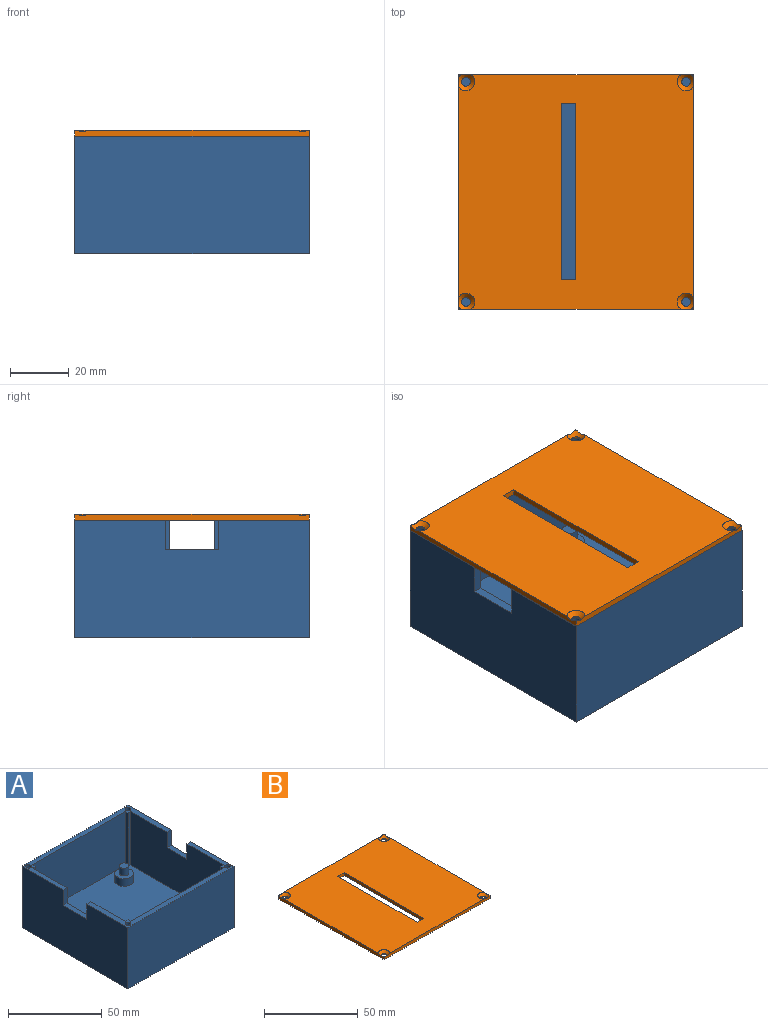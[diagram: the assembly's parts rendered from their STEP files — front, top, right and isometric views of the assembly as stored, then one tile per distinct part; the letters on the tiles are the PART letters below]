
ASSEMBLY  parts=2 mates=1
PART A: 50 faces, bbox 80x80x40 mm
  f0: plane 80x32.5mm, normal (0,0,1), area 406.4mm2, adj f1,f2,f4,f5,f6,f9,f10,f11
  f1: plane 80x40mm, normal (1,0,0), area 3050mm2, adj f0,f3,f5,f7,f8,f31,f32,f33
  f2: plane 70x35mm, normal (-1,0,0), area 2300mm2, adj f0,f3,f9,f18,f19,f31,f32,f33
  f3: plane 80x32.5mm, normal (0,0,1), area 406.4mm2, adj f1,f2,f4,f6,f7,f14,f15,f16
  f4: plane 70x35mm, normal (1,0,0), area 2270mm2, adj f0,f3,f13,f14,f19,f28,f29,f30
  f5: plane 80x40mm, normal (0,1,0), area 3200mm2, adj f0,f1,f6,f8
  f6: plane 80x40mm, normal (-1,0,0), area 3020mm2, adj f0,f3,f5,f7,f8,f28,f29,f30
  f7: plane 80x40mm, normal (0,-1,0), area 3200mm2, adj f1,f3,f6,f8
  f8: plane 80x80mm, normal (0,0,-1), area 6400mm2, adj f1,f5,f6,f7
  f9: plane 35x2mm, normal (0,-1,0), area 70mm2, adj f0,f2,f10,f19
  f10: plane 35x2mm, normal (-1,0,0), area 70mm2, adj f0,f9,f11,f19
  f11: plane 70x35mm, normal (0,-1,0), area 2450mm2, adj f0,f10,f12,f19
  f12: plane 35x2mm, normal (1,0,0), area 70mm2, adj f0,f11,f13,f19
  f13: plane 35x2mm, normal (0,-1,0), area 70mm2, adj f0,f4,f12,f19
  f14: plane 35x2mm, normal (0,1,0), area 70mm2, adj f3,f4,f15,f19
  f15: plane 35x2mm, normal (1,0,0), area 70mm2, adj f3,f14,f16,f19
  f16: plane 70x35mm, normal (0,1,0), area 2450mm2, adj f3,f15,f17,f19
  f17: plane 35x2mm, normal (-1,0,0), area 70mm2, adj f3,f16,f18,f19
  f18: plane 35x2mm, normal (0,1,0), area 70mm2, adj f2,f3,f17,f19
  f19: plane 74x74mm, normal (0,0,1), area 5145.8mm2, adj f2,f4,f9,f10,f11,f12,f13,f14
  f20: cylinder r=1.5mm len=9mm, axis (0,0,1), area 84.8mm2, adj f0,f21
  f21: plane 3x3mm, normal (0,0,1), area 7.1mm2, adj f20
  f22: cylinder r=1.5mm len=9mm, axis (0,0,1), area 84.8mm2, adj f3,f23
  f23: plane 3x3mm, normal (0,0,1), area 7.1mm2, adj f22
  f24: cylinder r=1.5mm len=9mm, axis (0,0,1), area 84.8mm2, adj f3,f25
  f25: plane 3x3mm, normal (0,0,1), area 7.1mm2, adj f24
  f26: cylinder r=1.5mm len=9mm, axis (0,0,1), area 84.8mm2, adj f0,f27
  f27: plane 3x3mm, normal (0,0,1), area 7.1mm2, adj f26
  f28: plane 10x3mm, normal (0,1,0), area 30mm2, adj f3,f4,f6,f30
  f29: plane 10x3mm, normal (0,-1,0), area 30mm2, adj f0,f4,f6,f30
  f30: plane 18x3mm, normal (0,0,1), area 54mm2, adj f4,f6,f28,f29
  f31: plane 10x3mm, normal (0,-1,0), area 30mm2, adj f0,f1,f2,f33
  f32: plane 10x3mm, normal (0,1,0), area 30mm2, adj f1,f2,f3,f33
  f33: plane 15x3mm, normal (0,0,1), area 45mm2, adj f1,f2,f31,f32
  f34: cylinder r=5mm len=10mm, axis (0,0,-1), area 157.1mm2, adj f19,f35
  f35: plane 10x10mm, normal (0,0,1), area 58.9mm2, adj f34,f42
  f36: cylinder r=5mm len=10mm, axis (0,0,-1), area 157.1mm2, adj f19,f37
  f37: plane 10x10mm, normal (0,0,1), area 58.9mm2, adj f36,f44
  f38: cylinder r=5mm len=10mm, axis (0,0,-1), area 157.1mm2, adj f19,f39
  f39: plane 10x10mm, normal (0,0,1), area 58.9mm2, adj f38,f46
  f40: cylinder r=5mm len=10mm, axis (0,0,-1), area 157.1mm2, adj f19,f41
  f41: plane 10x10mm, normal (0,0,1), area 58.9mm2, adj f40,f48
  f42: cylinder r=2.5mm len=5mm, axis (0,0,-1), area 78.5mm2, adj f35,f43
  f43: plane 5x5mm, normal (0,0,1), area 19.6mm2, adj f42
  f44: cylinder r=2.5mm len=5mm, axis (0,0,-1), area 78.5mm2, adj f37,f45
  f45: plane 5x5mm, normal (0,0,1), area 19.6mm2, adj f44
  f46: cylinder r=2.5mm len=5mm, axis (0,0,-1), area 78.5mm2, adj f39,f47
  f47: plane 5x5mm, normal (0,0,1), area 19.6mm2, adj f46
  f48: cylinder r=2.5mm len=5mm, axis (0,0,-1), area 78.5mm2, adj f41,f49
  f49: plane 5x5mm, normal (0,0,1), area 19.6mm2, adj f48
PART B: 22 faces, bbox 81x81x2 mm
  f0: plane 0.84x0.84mm, normal (0,0,1), area 0.3mm2, adj f4,f7,f14
  f1: plane 80x80mm, normal (0,0,1), area 5994.7mm2, adj f4,f5,f6,f7,f14,f15,f16,f17
  f2: plane 0.84x0.84mm, normal (0,0,1), area 0.3mm2, adj f6,f7,f15
  f3: plane 0.84x0.84mm, normal (0,0,1), area 0.3mm2, adj f5,f6,f16
  f4: plane 80x2mm, normal (0,1,0), area 157.8mm2, adj f0,f1,f5,f7,f8,f9,f14,f17
  f5: plane 80x2mm, normal (-1,0,0), area 157.8mm2, adj f1,f3,f4,f6,f8,f9,f16,f17
  f6: plane 80x2mm, normal (0,-1,0), area 157.8mm2, adj f1,f2,f3,f5,f7,f9,f15,f16
  f7: plane 80x2mm, normal (1,0,0), area 157.8mm2, adj f0,f1,f2,f4,f6,f9,f14,f15
  f8: plane 0.84x0.84mm, normal (0,0,1), area 0.3mm2, adj f4,f5,f17
  f9: plane 80x80mm, normal (0,0,-1), area 6071.7mm2, adj f4,f5,f6,f7,f10,f11,f12,f13
  f10: cylinder r=1.5mm len=3mm, axis (0,0,1), area 4.7mm2, adj f9,f17
  f11: cylinder r=1.5mm len=3mm, axis (0,0,1), area 4.7mm2, adj f9,f14
  f12: cylinder r=1.5mm len=3mm, axis (0,0,1), area 4.7mm2, adj f9,f15
  f13: cylinder r=1.5mm len=3mm, axis (0,0,1), area 4.7mm2, adj f9,f16
  f14: cone r=1.5mm half-angle=45deg, axis (0,0,1), area 26.8mm2, adj f0,f1,f4,f7,f11
  f15: cone r=1.5mm half-angle=45deg, axis (0,0,1), area 26.8mm2, adj f1,f2,f6,f7,f12
  f16: cone r=1.5mm half-angle=45deg, axis (0,0,1), area 26.8mm2, adj f1,f3,f5,f6,f13
  f17: cone r=1.5mm half-angle=45deg, axis (0,0,1), area 26.8mm2, adj f1,f4,f5,f8,f10
  f18: plane 60x2mm, normal (1,0,0), area 120mm2, adj f1,f9,f19,f21
  f19: plane 5x2mm, normal (0,1,0), area 10mm2, adj f1,f9,f18,f20
  f20: plane 60x2mm, normal (-1,0,0), area 120mm2, adj f1,f9,f19,f21
  f21: plane 5x2mm, normal (0,-1,0), area 10mm2, adj f1,f9,f18,f20
PLACE A t=(176.46,158.13,-38.14)mm
PLACE B t=(74.16,166.17,1.86)mm
MATE slider B.f13 <-> A.f24  axis (0,0,-1) through (138.96,120.63,1.86)mm
